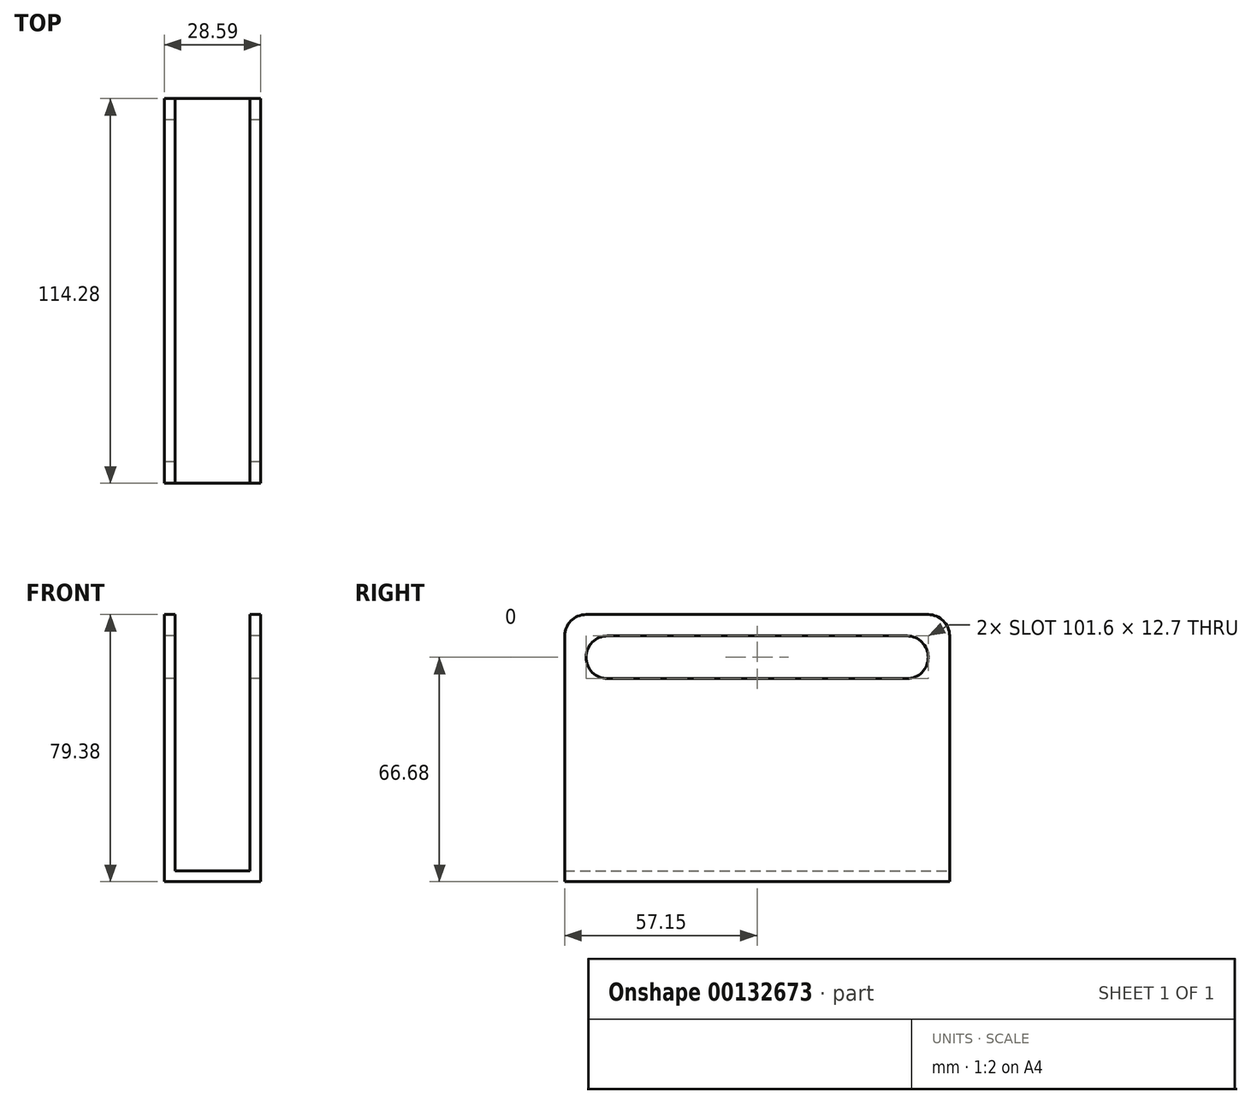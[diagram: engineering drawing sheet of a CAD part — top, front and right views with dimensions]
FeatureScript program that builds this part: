
annotation { "Feature Type Name" : "Feature", "Feature Type Description" : "" }
export const myFeature = defineFeature(function(context is Context, id is Id, definition is map)
    precondition{}
    {
        {
            var Q0;
            Q0=qCreatedBy(makeId("Right.planeOp"),FACE);
            var sketch = newSketch(context, id + "F0", { "sketchPlane" : qUnion([Q0])});
            skPoint(sketch, "E0", {"position": v(0, 0) * mm});
            skLineSegment(sketch, "E1.top", {"start": v(-6.37, 88.9) * mm, "end": v(95.23, 88.9) * mm});
            skLineSegment(sketch, "E1.left", {"start": v(-12.7, 12.7) * mm, "end": v(-12.7, 82.55) * mm});
            skArc(sketch, "E2", {"start": v(0, 82.55) * mm, "mid": v(-6.35, 76.2) * mm, "end": v(0, 69.85) * mm});
            skLineSegment(sketch, "E3.bottom", {"start": v(0, 82.55) * mm, "end": v(88.9, 82.55) * mm});
            skLineSegment(sketch, "E3.top", {"start": v(0, 69.85) * mm, "end": v(88.9, 69.85) * mm});
            skArc(sketch, "E4", {"start": v(88.9, 69.85) * mm, "mid": v(95.25, 76.2) * mm, "end": v(88.9, 82.55) * mm});
            skArc(sketch, "E5", {"start": v(-6.37, 88.9) * mm, "mid": v(-10.85, 87.03) * mm, "end": v(-12.7, 82.55) * mm});
            skArc(sketch, "E6", {"start": v(101.58, 82.55) * mm, "mid": v(99.72, 87.04) * mm, "end": v(95.23, 88.9) * mm});
            skLineSegment(sketch, "E7", {"start": v(101.58, 82.55) * mm, "end": v(101.58, 12.7) * mm});
            skLineSegment(sketch, "E8", {"start": v(-12.7, 12.7) * mm, "end": v(101.58, 12.7) * mm});
            skSolve(sketch);
        }
        {
            var Q0;
            Q0=makeQuery(id+"F0.imprint","IMPRINT",FACE,{"disambiguationData":[TD([[makeQuery(id+"F0.imprint","IMPRINT",EDGE,{"derivedFrom":sQuery(id+"F0.wireOp",EDGE,"E1.bottom")}),1.0]])]});
            var Q1;
            Q1=makeQuery(id+"F0.imprint","IMPRINT",FACE,{"disambiguationData":[TD([[makeQuery(id+"F0.imprint","IMPRINT",EDGE,{"derivedFrom":sQuery(id+"F0.wireOp",EDGE,"E1.top")}),-1.0]])]});
            extrude(context, id + "F1", {"entities" : qUnion([Q0, Q1]), "depth" : 3.17 * mm});
        }
        {
            var Q0;
            Q0=makeQuery(id+"F1.opExtrude","SWEPT_BODY",BODY,{"disambiguationData":[OSD([sQuery(id+"F0.wireOp",EDGE,"E1.bottom"),sQuery(id+"F0.wireOp",EDGE,"E1.top"),sQuery(id+"F0.wireOp",EDGE,"E1.left"),sQuery(id+"F0.wireOp",EDGE,"E1.right"),sQuery(id+"F0.wireOp",EDGE,"E2"),sQuery(id+"F0.wireOp",EDGE,"E3.bottom"),sQuery(id+"F0.wireOp",EDGE,"E3.top"),sQuery(id+"F0.wireOp",EDGE,"E4"),sQuery(id+"F0.wireOp",EDGE,"xA8DBkUA-NwmT-IRmx-fQ0t-vLBoeiS0nUHW"),sQuery(id+"F0.wireOp",EDGE,"8s5jRt50-C7tt-vZux-sj3g-W0TjklUS7moo"),sQuery(id+"F0.wireOp",EDGE,"3grR1sod-i6sn-W2vZ-G2zw-xfX1vCl78bIk")])]});
            var Q1;
            Q1=makeQuery(id+"F1.opExtrude","CAP_FACE",FACE,{"disambiguationData":[OSD([sQuery(id+"F0.wireOp",EDGE,"E1.bottom"),sQuery(id+"F0.wireOp",EDGE,"E1.top"),sQuery(id+"F0.wireOp",EDGE,"E1.left"),sQuery(id+"F0.wireOp",EDGE,"E1.right"),sQuery(id+"F0.wireOp",EDGE,"E2"),sQuery(id+"F0.wireOp",EDGE,"E3.bottom"),sQuery(id+"F0.wireOp",EDGE,"E3.top"),sQuery(id+"F0.wireOp",EDGE,"E4"),sQuery(id+"F0.wireOp",EDGE,"xA8DBkUA-NwmT-IRmx-fQ0t-vLBoeiS0nUHW"),sQuery(id+"F0.wireOp",EDGE,"8s5jRt50-C7tt-vZux-sj3g-W0TjklUS7moo"),sQuery(id+"F0.wireOp",EDGE,"3grR1sod-i6sn-W2vZ-G2zw-xfX1vCl78bIk")])],"isStart":true});
            transform(context, id + "F2", {"entities" : qUnion([Q0]), "transformType" : TransformType.TRANSLATION_DISTANCE, "transformDirection" : qUnion([Q1]), "distance" : 25.4 * mm, "makeCopy" : true});
        }
        {
            var Q0;
            Q0=makeQuery(id+"F1.opExtrude","SWEPT_FACE",FACE,{"disambiguationData":[OSD([sQuery(id+"F0.wireOp",EDGE,"E8")])]});
            var sketch = newSketch(context, id + "F3", { "sketchPlane" : qUnion([Q0])});
            skLineSegment(sketch, "E9.bottom", {"start": v(3.18, 12.7) * mm, "end": v(-25.41, 12.7) * mm});
            skLineSegment(sketch, "E9.top", {"start": v(3.18, -101.58) * mm, "end": v(-25.41, -101.58) * mm});
            skLineSegment(sketch, "E9.left", {"start": v(3.18, 12.7) * mm, "end": v(3.18, -101.58) * mm});
            skLineSegment(sketch, "E9.right", {"start": v(-25.41, 12.7) * mm, "end": v(-25.41, -101.58) * mm});
            skSolve(sketch);
        }
        {
            var Q0;
            {var subQ3=sQuery(id+"F3.wireOp",EDGE,"E9.right");Q0=makeQuery(id+"F3.imprint","IMPRINT",FACE,{"disambiguationData":[TD([[makeQuery(id+"F3.imprint","IMPRINT",EDGE,{"derivedFrom":subQ3}),1.0]])]});}
            var Q1;
            {var subQ4=sQuery(id+"F3.wireOp",EDGE,"E9.left");Q1=makeQuery(id+"F3.imprint","IMPRINT",FACE,{"disambiguationData":[TD([[makeQuery(id+"F3.imprint","IMPRINT",EDGE,{"derivedFrom":subQ4}),-1.0]])]});}
            extrude(context, id + "F4", {"entities" : qUnion([Q0, Q1]), "operationType" : NewBodyOperationType.ADD, "depth" : 3.17 * mm});
        }
    });
